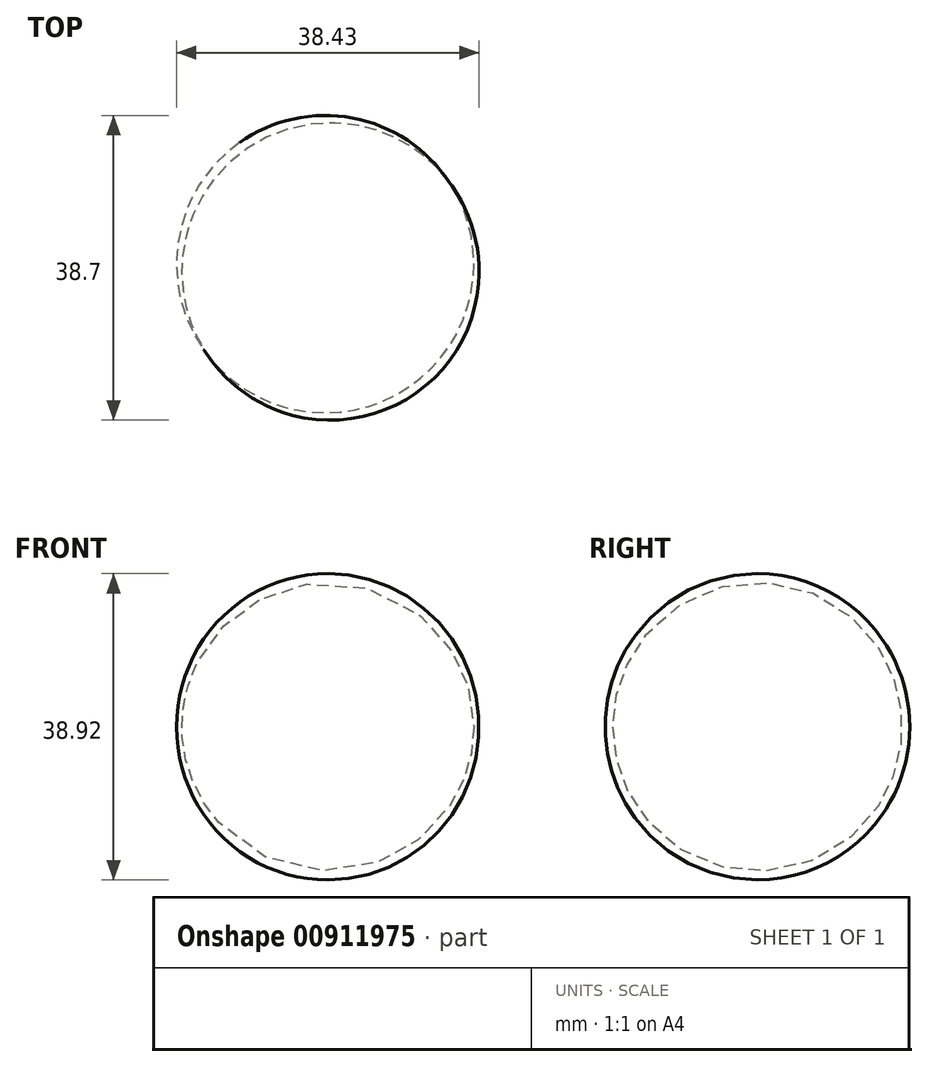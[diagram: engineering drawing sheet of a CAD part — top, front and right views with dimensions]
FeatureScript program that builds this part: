
annotation { "Feature Type Name" : "Feature", "Feature Type Description" : "" }
export const myFeature = defineFeature(function(context is Context, id is Id, definition is map)
    precondition{}
    {
        {
            var Q0;
            Q0=qCreatedBy(makeId("Top.planeOp"),FACE);
            var sketch = newSketch(context, id + "F0", { "sketchPlane" : qUnion([Q0])});
            skArc(sketch, "E0", {"start": v(0, 21.78) * mm, "mid": v(-26.64, 26.78) * mm, "end": v(-30.83, 0) * mm});
            skLineSegment(sketch, "E1", {"start": v(0, 21.78) * mm, "end": v(-30.83, 0) * mm});
            skSolve(sketch);
        }
        {
            var Q0;
            Q0=makeQuery(id+"F0.imprint","IMPRINT",FACE,{"disambiguationData":[TD([[makeQuery(id+"F0.imprint","IMPRINT",EDGE,{"derivedFrom":sQuery(id+"F0.wireOp",EDGE,"E0")}),1.0]])]});
            var Q1;
            Q1=sQuery(id+"F0.wireOp",EDGE,"E1");
            revolve(context, id + "F1", {"surfaceOperationType" : NewSurfaceOperationType.NEW, "entities" : qUnion([Q0]), "axis" : qUnion([Q1]), "revolveType" : RevolveType.FULL});
        }
    });
